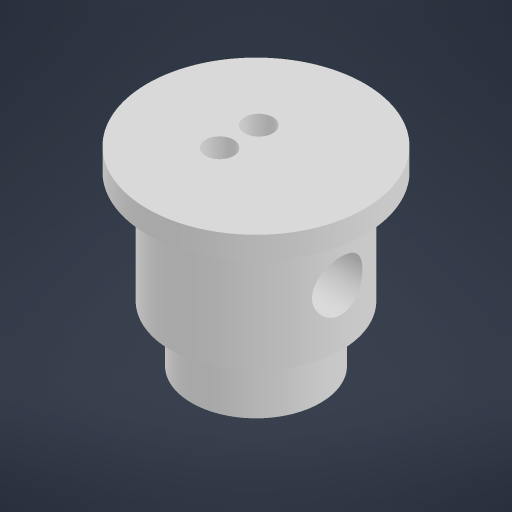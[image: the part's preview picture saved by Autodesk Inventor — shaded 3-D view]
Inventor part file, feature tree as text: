
AUTODESK INVENTOR PART (.ipt)
format: ipt  version: 2024.1 (Build 281209000, 209)  size: 212,480 bytes
history: native  units: mm
features: extrude x6, sketch x4
ambient origin geometry x8: Origin, YZ Plane, XZ Plane, XY Plane, X Axis, Y Axis, Z Axis, Center Point
bodies: Solid1 (feature_tree)
feature tree (10):
  sketch  "Sketch1"  dims[d0=15.2mm d1=19.4mm]
  extrude  "Extrusion1"  Depth=19.4mm
  extrude  "Extrusion2"  Depth=10.0mm TaperAngle=0.0deg
  extrude  "Extrusion3"  Depth=5.0mm
  extrude  "Extrusion4"  Depth=10.0mm
  sketch  "Sketch6"  dims[d8=23.0mm d9=0.0mm d10=7.5mm d11=2.0mm d12=5.0mm d13=0.0mm d18=2.5mm d19=10.0mm d20=0.0mm d24=3.5mm d25=1.5mm d26=10.0mm d27=0.0mm d21=0.5mm d22=0.872665mm d23=0.5mm]
  extrude  "Extrusion6"  Depth=10.0mm
  extrude  "Extrusion8"  Depth=5.0mm TaperAngle=0.0deg
  sketch  "Sketch2"  dims[d2=2.0mm d3=0.0mm d4=10.0mm d5=0.0mm]
  sketch  "Sketch3"  dims[d6=4.5mm d7=5.0mm]
